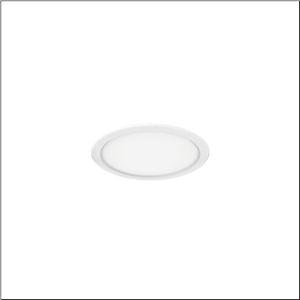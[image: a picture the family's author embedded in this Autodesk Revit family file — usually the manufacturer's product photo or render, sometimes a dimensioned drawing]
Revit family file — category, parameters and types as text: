
# Revit family: lunis_41_eco_51ds107d33a
name_source: partatom
category: Lighting Fixtures
units: mm (PartAtom-declared; Revit-internal decimal feet)

## family parameters
Cut with Voids When Loaded = No
Host = Face
Light Source = No
Part Type = Normal
Room Calculation Point = No
Round Connector Dimension = Use Diameter
Shared = No

## types (1)
- Lunis 41 ECO (1 x LED, 1400 lm, 14 W, 3000K)
    Apparent Load = 14 VA
    CIE Flux Codes = 47 80 97 100 100
    Color Rendering = 80
    Color Temperature = 3000K
    Default Elevation = 1800 mm
    Description = Lunis 41,  ECO, downlight, light emission: direct distribution, LED rated luminous flux: 1.400lm, light colour: 830, control gear: ECG, mains connection: 230V, AC, 50/60Hz, housing, round, of aluminium, coated, traffic white (RAL 9016), diameter: 166mm, recess depth: 54mm, protection rating (complete): IP20, protection rating (on room side): IP40, insulation class (complete): insulation class II (safety insulation), certification: CE, permissible ambient temperature for indoor applications: -20..+40°C, packaging unit: 1 piece
    Height = 0 mm  [stored 0 ft]
    Lamp = 1 x LED
    Lamp Light Flux = 1400 lm
    Lamp Power = 14 W
    Lamp count = 1
    Length = 165 mm
    Luminous efficacy = 100 lm/W
    Manufacturer = Siteco
    ModVariant = No
    Model = 51DS107D33A
    Mounting Place = Ceiling
    Mounting Type = Recessed
    Number of Poles = 1
    OnlyDefault = Yes
    Power Factor = 1
    Product Name = Lunis 41 ECO
    Product group = downlight
    ProductGroupID = 400
    Protection Class = Protection class II
    Protection Degree = IP 20
    RLX_Detail_Level = 1
    RLX_Emergency_Light_Flux = 0 lm
    RLX_Emergency_Type = 0
    RLX_Emergency_Type_DB = No
    RlxData = <blob elided: 25717 chars, md5=84a231fe>
    Socket = socket
    Standby Power = 0 W
    System Light Flux = 1400 lm
    System Power = 14 W
    Type Comments = Product without accessories
    Type Image = l_1007041.jpg
    URL = http://relux.com
    VarID = ---
    Voltage = 0 V
    Weight = 0.00 kg
    Width = 0 mm  [stored 0 ft]

note: [stored X ft] marks values corroborated as IEEE doubles in the binary element streams (Revit-internal decimal feet)

## geometry (parser evidence)
native form markers: Blend x4, Sweep x11
no freeform markers — native parametric forms only
